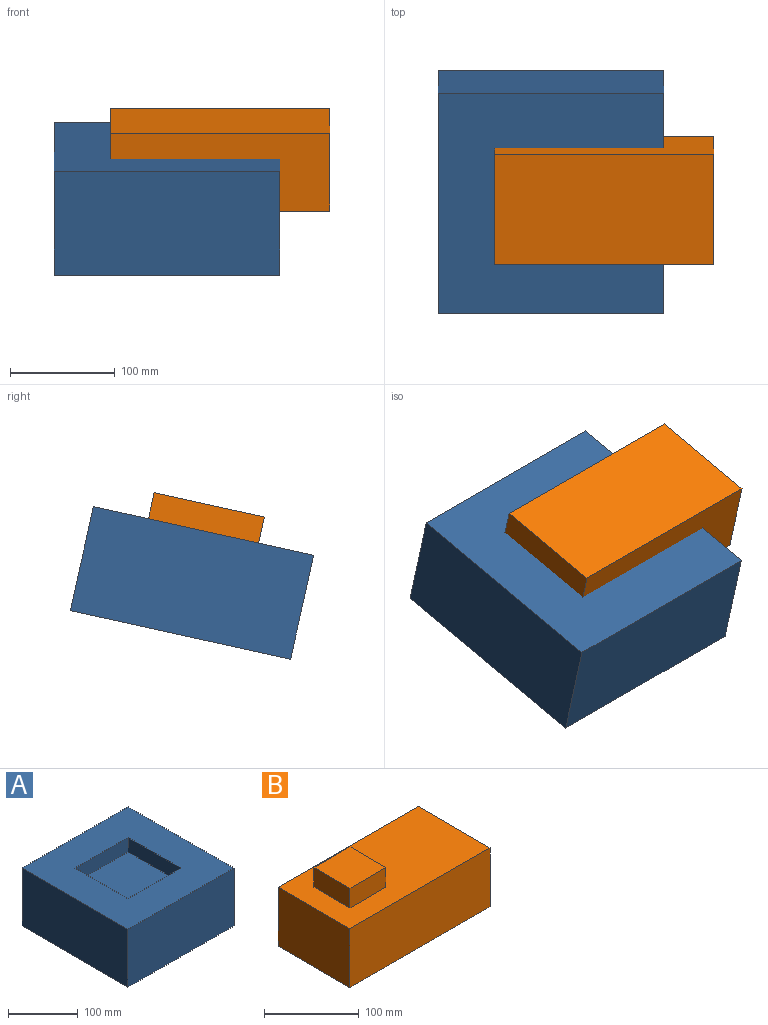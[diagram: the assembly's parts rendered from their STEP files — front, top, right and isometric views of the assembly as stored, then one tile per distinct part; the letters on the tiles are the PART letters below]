
ASSEMBLY  parts=2 mates=1
PART A: 11 faces, bbox 215.1x215.1x101.6 mm
  f0: plane 107.57x25.4mm, normal (0,-1,0), area 2732.3mm2, adj f1,f7,f8,f10
  f1: plane 107.57x25.4mm, normal (-1,0,0), area 2732.3mm2, adj f0,f2,f8,f10
  f2: plane 107.57x25.4mm, normal (0,1,0), area 2732.3mm2, adj f1,f7,f8,f10
  f3: plane 215.14x101.6mm, normal (1,0,0), area 21858mm2, adj f4,f6,f8,f9
  f4: plane 215.14x101.6mm, normal (0,1,0), area 21858mm2, adj f3,f5,f8,f9
  f5: plane 215.14x101.6mm, normal (-1,0,0), area 21858mm2, adj f4,f6,f8,f9
  f6: plane 215.14x101.6mm, normal (0,-1,0), area 21858mm2, adj f3,f5,f8,f9
  f7: plane 107.57x25.4mm, normal (1,0,0), area 2732.3mm2, adj f0,f2,f8,f10
  f8: plane 215.14x215.14mm, normal (0,0,1), area 34713.3mm2, adj f0,f1,f2,f3,f4,f5,f6,f7
  f9: plane 215.14x215.14mm, normal (0,0,-1), area 46284.4mm2, adj f3,f4,f5,f6
  f10: plane 107.57x107.57mm, normal (0,0,1), area 11571.1mm2, adj f0,f1,f2,f7
PART B: 11 faces, bbox 209.2x107.6x101.6 mm
  f0: plane 53.78x25.4mm, normal (1,0,0), area 1366.1mm2, adj f1,f3,f4,f8
  f1: plane 53.78x25.4mm, normal (0,1,0), area 1366.1mm2, adj f0,f2,f4,f8
  f2: plane 53.78x25.4mm, normal (-1,0,0), area 1366.1mm2, adj f1,f3,f4,f8
  f3: plane 53.78x25.4mm, normal (0,-1,0), area 1366.1mm2, adj f0,f2,f4,f8
  f4: plane 53.78x53.78mm, normal (0,0,1), area 2892.5mm2, adj f0,f1,f2,f3
  f5: plane 209.16x76.2mm, normal (0,1,0), area 15938.3mm2, adj f6,f8,f9,f10
  f6: plane 107.56x76.2mm, normal (-1,0,0), area 8196.4mm2, adj f5,f7,f8,f9
  f7: plane 209.16x76.2mm, normal (0,-1,0), area 15938.3mm2, adj f6,f8,f9,f10
  f8: plane 209.16x107.56mm, normal (0,0,1), area 19606.1mm2, adj f0,f1,f2,f3,f5,f6,f7,f10
  f9: plane 209.16x107.56mm, normal (0,0,-1), area 22498.6mm2, adj f5,f6,f7,f10
  f10: plane 107.56x76.2mm, normal (1,0,0), area 8196.4mm2, adj f5,f7,f8,f9
PLACE A rot(axis=(-1,0,0),167.5deg) t=(-21.45,-162.38,100.83)mm
PLACE B rot(axis=(-1,0,0),167.5deg) t=(-21.45,-167.86,125.63)mm
MATE fastened A.f10 <-> B.f4  axis (0,0.22,-0.98) through (-21.45,-145.94,26.42)mm
